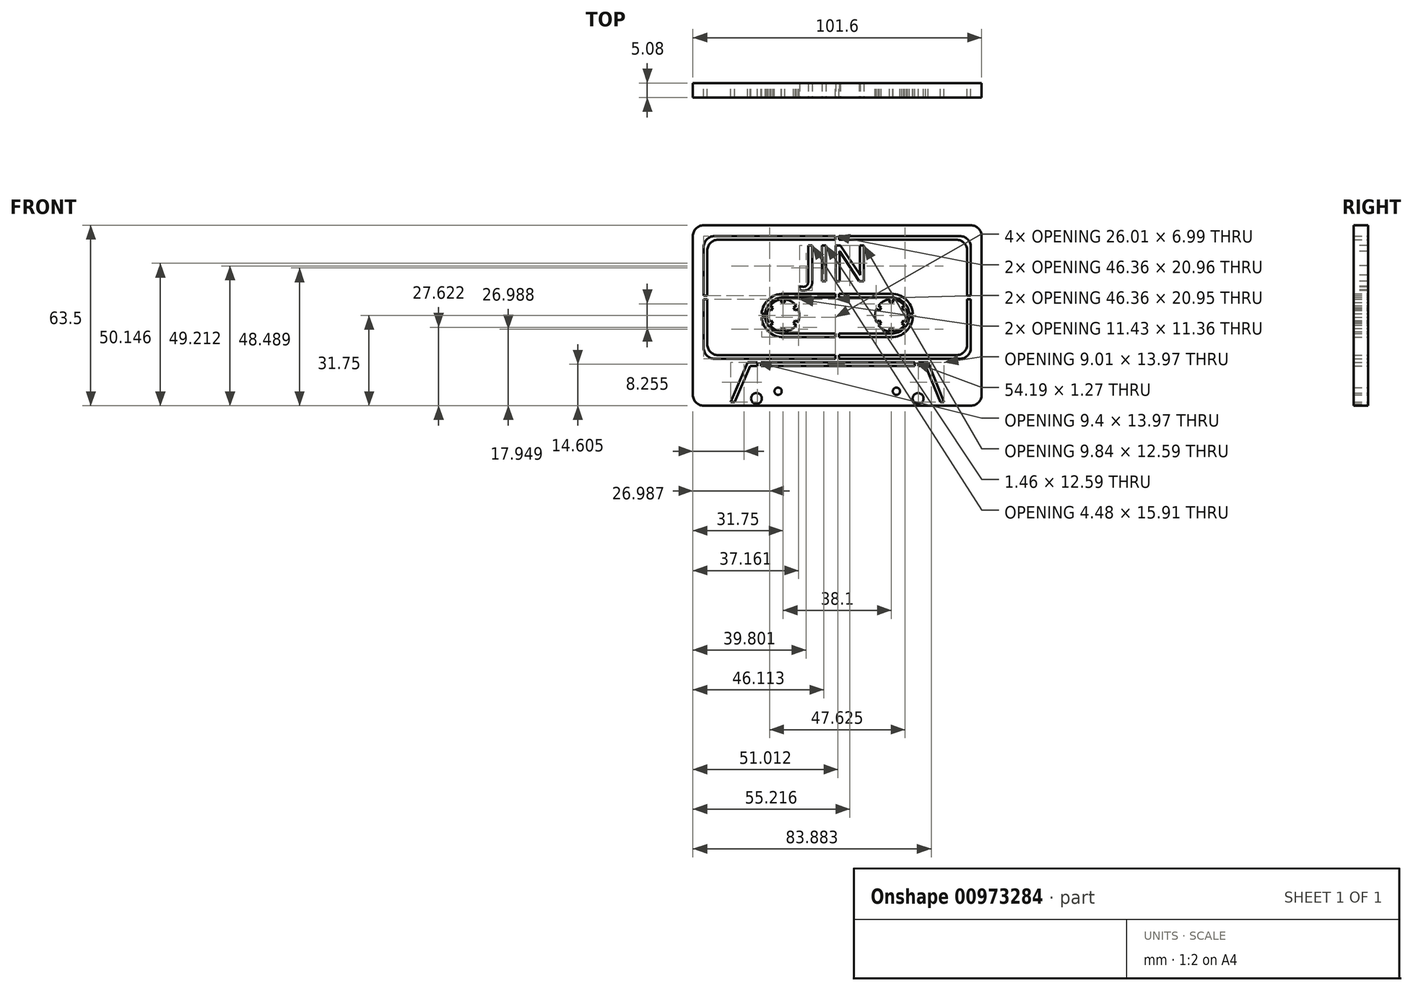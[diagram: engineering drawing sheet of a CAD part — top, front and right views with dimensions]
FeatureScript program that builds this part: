
annotation { "Feature Type Name" : "Feature", "Feature Type Description" : "" }
export const myFeature = defineFeature(function(context is Context, id is Id, definition is map)
    precondition{}
    {
        {
            var Q0;
            Q0=qCreatedBy(makeId("Front.planeOp"),FACE);
            var sketch = newSketch(context, id + "F0", { "sketchPlane" : qUnion([Q0])});
            skLineSegment(sketch, "E0.bottom", {"start": v(47, 31.75) * mm, "end": v(-47, 31.75) * mm});
            skLineSegment(sketch, "E0.top", {"start": v(47, -31.75) * mm, "end": v(-47, -31.75) * mm});
            skLineSegment(sketch, "E0.left", {"start": v(50.8, 27.94) * mm, "end": v(50.8, -27.94) * mm});
            skLineSegment(sketch, "E0.right", {"start": v(-50.8, 27.94) * mm, "end": v(-50.8, -27.94) * mm});
            skPoint(sketch, "E0.middle", {"position": v(0, 0) * mm});
            skPoint(sketch, "E1.visualSharp", {"position": v(50.8, 31.75) * mm});
            skArc(sketch, "E1.filletArc", {"start": v(50.8, 27.94) * mm, "mid": v(49.68, 30.63) * mm, "end": v(47, 31.75) * mm});
            skPoint(sketch, "E2.visualSharp", {"position": v(-50.8, 31.75) * mm});
            skArc(sketch, "E2.filletArc", {"start": v(-47, 31.75) * mm, "mid": v(-49.68, 30.63) * mm, "end": v(-50.8, 27.94) * mm});
            skPoint(sketch, "E3.visualSharp", {"position": v(-50.8, -31.75) * mm});
            skArc(sketch, "E3.filletArc", {"start": v(-50.8, -27.94) * mm, "mid": v(-49.68, -30.63) * mm, "end": v(-47, -31.75) * mm});
            skPoint(sketch, "E4.visualSharp", {"position": v(50.8, -31.75) * mm});
            skArc(sketch, "E4.filletArc", {"start": v(47, -31.75) * mm, "mid": v(49.68, -30.63) * mm, "end": v(50.8, -27.94) * mm});
            skLineSegment(sketch, "E5.bottom", {"start": v(-43.18, 27.94) * mm, "end": v(-0.64, 27.94) * mm});
            skLineSegment(sketch, "E5.top", {"start": v(-43.18, -15.24) * mm, "end": v(-0.64, -15.24) * mm});
            skLineSegment(sketch, "E5.left", {"start": v(-47, 24.13) * mm, "end": v(-47, 6.98) * mm});
            skLineSegment(sketch, "E5.right", {"start": v(47, 24.13) * mm, "end": v(47, 6.99) * mm});
            skLineSegment(sketch, "E6.bottom", {"start": v(-41.91, 26.67) * mm, "end": v(-0.63, 26.67) * mm});
            skLineSegment(sketch, "E6.top", {"start": v(-41.91, -13.97) * mm, "end": v(-0.63, -13.97) * mm});
            skLineSegment(sketch, "E6.left", {"start": v(-45.72, 22.86) * mm, "end": v(-45.72, 6.98) * mm});
            skLineSegment(sketch, "E6.right", {"start": v(45.72, 22.86) * mm, "end": v(45.72, 6.99) * mm});
            skArc(sketch, "E7.filletArc", {"start": v(47, 24.13) * mm, "mid": v(45.87, 26.82) * mm, "end": v(43.18, 27.94) * mm});
            skPoint(sketch, "E8.visualSharp", {"position": v(45.72, 26.67) * mm});
            skArc(sketch, "E8.filletArc", {"start": v(45.72, 22.86) * mm, "mid": v(44.6, 25.55) * mm, "end": v(41.91, 26.67) * mm});
            skPoint(sketch, "E9.visualSharp", {"position": v(47, -15.24) * mm});
            skArc(sketch, "E9.filletArc", {"start": v(43.18, -15.24) * mm, "mid": v(45.87, -14.12) * mm, "end": v(47, -11.43) * mm});
            skPoint(sketch, "E10.visualSharp", {"position": v(45.72, -13.97) * mm});
            skArc(sketch, "E10.filletArc", {"start": v(41.91, -13.97) * mm, "mid": v(44.6, -12.85) * mm, "end": v(45.72, -10.16) * mm});
            skPoint(sketch, "E11.visualSharp", {"position": v(-47, -15.24) * mm});
            skArc(sketch, "E11.filletArc", {"start": v(-47, -11.43) * mm, "mid": v(-45.87, -14.12) * mm, "end": v(-43.18, -15.24) * mm});
            skPoint(sketch, "E12.visualSharp", {"position": v(-45.72, -13.97) * mm});
            skArc(sketch, "E12.filletArc", {"start": v(-45.72, -10.16) * mm, "mid": v(-44.6, -12.85) * mm, "end": v(-41.91, -13.97) * mm});
            skArc(sketch, "E13.filletArc", {"start": v(-43.18, 27.94) * mm, "mid": v(-45.87, 26.82) * mm, "end": v(-47, 24.13) * mm});
            skPoint(sketch, "E14.visualSharp", {"position": v(-45.72, 26.67) * mm});
            skArc(sketch, "E14.filletArc", {"start": v(-41.91, 26.67) * mm, "mid": v(-44.6, 25.55) * mm, "end": v(-45.72, 22.86) * mm});
            skLineSegment(sketch, "E15", {"start": v(0.64, -15.24) * mm, "end": v(0.64, -13.97) * mm});
            skLineSegment(sketch, "E16", {"start": v(-0.64, -15.24) * mm, "end": v(-0.64, -13.97) * mm});
            skLineSegment(sketch, "E17.trimOffspring", {"start": v(-0.64, 26.67) * mm, "end": v(-0.64, 27.94) * mm});
            skLineSegment(sketch, "E18.trimOffspring", {"start": v(0.64, 26.67) * mm, "end": v(0.64, 27.94) * mm});
            skLineSegment(sketch, "E19.trimOffspring", {"start": v(0.63, -13.97) * mm, "end": v(41.91, -13.97) * mm});
            skLineSegment(sketch, "E20.trimOffspring", {"start": v(0.64, -15.24) * mm, "end": v(43.18, -15.24) * mm});
            skLineSegment(sketch, "E21.trimOffspring", {"start": v(0.64, 27.94) * mm, "end": v(43.18, 27.94) * mm});
            skLineSegment(sketch, "E22.trimOffspring", {"start": v(0.63, 26.67) * mm, "end": v(41.91, 26.67) * mm});
            skLineSegment(sketch, "E23", {"start": v(-47, 6.98) * mm, "end": v(-45.72, 6.99) * mm});
            skLineSegment(sketch, "E24", {"start": v(-47, 5.71) * mm, "end": v(-45.72, 5.71) * mm});
            skLineSegment(sketch, "E25.trimOffspring", {"start": v(45.72, 6.99) * mm, "end": v(47, 6.99) * mm});
            skLineSegment(sketch, "E26.trimOffspring", {"start": v(45.72, 5.72) * mm, "end": v(47, 5.72) * mm});
            skPoint(sketch, "E27.orphan", {"position": v(48.52, 5.72) * mm});
            skPoint(sketch, "E28.orphan", {"position": v(48.52, 6.99) * mm});
            skLineSegment(sketch, "E29.trimOffspring", {"start": v(47, 5.72) * mm, "end": v(47, -11.43) * mm});
            skLineSegment(sketch, "E30.trimOffspring", {"start": v(45.72, 5.72) * mm, "end": v(45.72, -10.16) * mm});
            skLineSegment(sketch, "E31.trimOffspring", {"start": v(-45.72, 5.71) * mm, "end": v(-45.72, -10.16) * mm});
            skLineSegment(sketch, "E32.trimOffspring", {"start": v(-47, 5.71) * mm, "end": v(-47, -11.43) * mm});
            skLineSegment(sketch, "E33.bottom", {"start": v(-19.05, 6.35) * mm, "end": v(-0.63, 6.35) * mm});
            skLineSegment(sketch, "E33.top", {"start": v(-19.05, -6.35) * mm, "end": v(-0.63, -6.35) * mm});
            skLineSegment(sketch, "E34.bottom", {"start": v(-19.05, 7.62) * mm, "end": v(-0.63, 7.62) * mm});
            skLineSegment(sketch, "E34.top", {"start": v(-19.05, -7.62) * mm, "end": v(-0.63, -7.62) * mm});
            skLineSegment(sketch, "E35", {"start": v(-0.63, 7.62) * mm, "end": v(-0.63, 6.35) * mm});
            skLineSegment(sketch, "E36", {"start": v(0.63, 7.62) * mm, "end": v(0.63, 6.35) * mm});
            skLineSegment(sketch, "E37.trimOffspring", {"start": v(-0.63, -6.35) * mm, "end": v(-0.63, -7.62) * mm});
            skLineSegment(sketch, "E38.trimOffspring", {"start": v(0.63, -6.35) * mm, "end": v(0.63, -7.62) * mm});
            skLineSegment(sketch, "E39.trimOffspring", {"start": v(0.64, -7.62) * mm, "end": v(19.05, -7.62) * mm});
            skLineSegment(sketch, "E40.trimOffspring", {"start": v(0.63, -6.35) * mm, "end": v(19.05, -6.35) * mm});
            skLineSegment(sketch, "E41.trimOffspring", {"start": v(0.63, 7.62) * mm, "end": v(19.05, 7.62) * mm});
            skLineSegment(sketch, "E42.trimOffspring", {"start": v(0.64, 6.35) * mm, "end": v(23.26, 6.35) * mm});
            skArc(sketch, "E43", {"start": v(-19.69, 5.68) * mm, "mid": v(-21.9, 4.95) * mm, "end": v(-23.65, 3.39) * mm});
            skArc(sketch, "E44", {"start": v(18.41, 5.68) * mm, "mid": v(16.2, 4.95) * mm, "end": v(14.45, 3.39) * mm});
            skArc(sketch, "E45", {"start": v(-19.05, 7.62) * mm, "mid": v(-24.2, 5.6) * mm, "end": v(-26.64, 0.64) * mm});
            skArc(sketch, "E46", {"start": v(-19.05, 6.35) * mm, "mid": v(-23.3, 4.7) * mm, "end": v(-25.37, 0.63) * mm});
            skArc(sketch, "E47", {"start": v(19.05, 7.62) * mm, "mid": v(24.2, 5.6) * mm, "end": v(26.64, 0.64) * mm});
            skArc(sketch, "E48", {"start": v(19.05, 6.35) * mm, "mid": v(23.3, 4.7) * mm, "end": v(25.37, 0.63) * mm});
            skLineSegment(sketch, "E49", {"start": v(-26.64, 0.64) * mm, "end": v(-25.37, 0.64) * mm});
            skLineSegment(sketch, "E50", {"start": v(-26.64, -0.64) * mm, "end": v(-25.37, -0.64) * mm});
            skArc(sketch, "E51.trimOffspring", {"start": v(-26.64, -0.64) * mm, "mid": v(-24.2, -5.6) * mm, "end": v(-19.05, -7.62) * mm});
            skArc(sketch, "E52.trimOffspring", {"start": v(-25.37, -0.64) * mm, "mid": v(-23.3, -4.7) * mm, "end": v(-19.05, -6.35) * mm});
            skLineSegment(sketch, "E53.trimOffspring", {"start": v(25.37, 0.64) * mm, "end": v(26.64, 0.64) * mm});
            skLineSegment(sketch, "E54.trimOffspring", {"start": v(25.37, -0.64) * mm, "end": v(26.64, -0.64) * mm});
            skArc(sketch, "E55.trimOffspring", {"start": v(25.37, -0.64) * mm, "mid": v(23.3, -4.7) * mm, "end": v(19.05, -6.35) * mm});
            skArc(sketch, "E56.trimOffspring", {"start": v(26.64, -0.64) * mm, "mid": v(24.2, -5.6) * mm, "end": v(19.05, -7.62) * mm});
            skLineSegment(sketch, "E57", {"start": v(-18.41, 5.68) * mm, "end": v(-18.41, 4.57) * mm});
            skLineSegment(sketch, "E58", {"start": v(-18.41, 4.57) * mm, "end": v(-19.69, 4.57) * mm});
            skLineSegment(sketch, "E59", {"start": v(-19.69, 4.57) * mm, "end": v(-19.69, 5.68) * mm});
            skLineSegment(sketch, "E60.MirrorCS", {"start": v(18.41, 5.68) * mm, "end": v(18.41, 4.57) * mm});
            skLineSegment(sketch, "E61.MirrorCS", {"start": v(18.41, 4.57) * mm, "end": v(19.69, 4.57) * mm});
            skLineSegment(sketch, "E62.MirrorCS", {"start": v(19.69, 4.57) * mm, "end": v(19.69, 5.68) * mm});
            skLineSegment(sketch, "E63.1.0", {"start": v(-23.65, 3.39) * mm, "end": v(-22.7, 2.84) * mm});
            skLineSegment(sketch, "E63.1.1", {"start": v(-22.7, 2.84) * mm, "end": v(-23.33, 1.74) * mm});
            skLineSegment(sketch, "E63.1.2", {"start": v(-23.33, 1.74) * mm, "end": v(-24.29, 2.29) * mm});
            skLineSegment(sketch, "E63.2.0", {"start": v(-24.29, -2.29) * mm, "end": v(-23.33, -1.74) * mm});
            skLineSegment(sketch, "E63.2.1", {"start": v(-23.33, -1.74) * mm, "end": v(-22.7, -2.84) * mm});
            skLineSegment(sketch, "E63.2.2", {"start": v(-22.7, -2.84) * mm, "end": v(-23.65, -3.39) * mm});
            skLineSegment(sketch, "E63.3.0", {"start": v(-19.69, -5.68) * mm, "end": v(-19.69, -4.57) * mm});
            skLineSegment(sketch, "E63.3.1", {"start": v(-19.69, -4.57) * mm, "end": v(-18.41, -4.57) * mm});
            skLineSegment(sketch, "E63.3.2", {"start": v(-18.41, -4.57) * mm, "end": v(-18.41, -5.68) * mm});
            skLineSegment(sketch, "E63.4.0", {"start": v(-14.45, -3.39) * mm, "end": v(-15.4, -2.84) * mm});
            skLineSegment(sketch, "E63.4.1", {"start": v(-15.4, -2.84) * mm, "end": v(-14.77, -1.74) * mm});
            skLineSegment(sketch, "E63.4.2", {"start": v(-14.77, -1.74) * mm, "end": v(-13.81, -2.29) * mm});
            skLineSegment(sketch, "E63.5.0", {"start": v(-13.81, 2.29) * mm, "end": v(-14.77, 1.74) * mm});
            skLineSegment(sketch, "E63.5.1", {"start": v(-14.77, 1.74) * mm, "end": v(-15.4, 2.84) * mm});
            skLineSegment(sketch, "E63.5.2", {"start": v(-15.4, 2.84) * mm, "end": v(-14.45, 3.39) * mm});
            skArc(sketch, "E64.trimOffspring", {"start": v(-14.45, 3.39) * mm, "mid": v(-16.2, 4.95) * mm, "end": v(-18.41, 5.68) * mm});
            skArc(sketch, "E65.trimOffspring", {"start": v(-13.81, -2.29) * mm, "mid": v(-13.33, 0) * mm, "end": v(-13.81, 2.29) * mm});
            skArc(sketch, "E66.trimOffspring", {"start": v(-18.41, -5.68) * mm, "mid": v(-16.2, -4.95) * mm, "end": v(-14.45, -3.39) * mm});
            skArc(sketch, "E67.trimOffspring", {"start": v(-23.65, -3.39) * mm, "mid": v(-21.9, -4.95) * mm, "end": v(-19.69, -5.68) * mm});
            skArc(sketch, "E68.trimOffspring", {"start": v(-24.29, 2.29) * mm, "mid": v(-24.77, 0) * mm, "end": v(-24.29, -2.29) * mm});
            skLineSegment(sketch, "E69.1.0", {"start": v(15.4, 2.84) * mm, "end": v(14.45, 3.39) * mm});
            skLineSegment(sketch, "E69.1.1", {"start": v(14.77, 1.74) * mm, "end": v(15.4, 2.84) * mm});
            skLineSegment(sketch, "E69.1.2", {"start": v(13.81, 2.29) * mm, "end": v(14.77, 1.74) * mm});
            skLineSegment(sketch, "E69.2.0", {"start": v(14.77, -1.74) * mm, "end": v(13.81, -2.29) * mm});
            skLineSegment(sketch, "E69.2.1", {"start": v(15.4, -2.84) * mm, "end": v(14.77, -1.74) * mm});
            skLineSegment(sketch, "E69.2.2", {"start": v(14.45, -3.39) * mm, "end": v(15.4, -2.84) * mm});
            skLineSegment(sketch, "E69.3.0", {"start": v(18.41, -4.57) * mm, "end": v(18.41, -5.68) * mm});
            skLineSegment(sketch, "E69.3.1", {"start": v(19.69, -4.57) * mm, "end": v(18.41, -4.57) * mm});
            skLineSegment(sketch, "E69.3.2", {"start": v(19.69, -5.68) * mm, "end": v(19.69, -4.57) * mm});
            skLineSegment(sketch, "E69.4.0", {"start": v(22.7, -2.84) * mm, "end": v(23.65, -3.39) * mm});
            skLineSegment(sketch, "E69.4.1", {"start": v(23.33, -1.74) * mm, "end": v(22.7, -2.84) * mm});
            skLineSegment(sketch, "E69.4.2", {"start": v(24.29, -2.29) * mm, "end": v(23.33, -1.74) * mm});
            skLineSegment(sketch, "E69.5.0", {"start": v(23.33, 1.74) * mm, "end": v(24.29, 2.29) * mm});
            skLineSegment(sketch, "E69.5.1", {"start": v(22.7, 2.84) * mm, "end": v(23.33, 1.74) * mm});
            skLineSegment(sketch, "E69.5.2", {"start": v(23.65, 3.39) * mm, "end": v(22.7, 2.84) * mm});
            skArc(sketch, "E70.trimOffspring", {"start": v(23.65, 3.39) * mm, "mid": v(21.9, 4.95) * mm, "end": v(19.69, 5.68) * mm});
            skArc(sketch, "E71.trimOffspring", {"start": v(24.29, -2.29) * mm, "mid": v(24.77, 0) * mm, "end": v(24.29, 2.29) * mm});
            skArc(sketch, "E72.trimOffspring", {"start": v(19.69, -5.68) * mm, "mid": v(21.9, -4.95) * mm, "end": v(23.65, -3.39) * mm});
            skArc(sketch, "E73.trimOffspring", {"start": v(14.45, -3.39) * mm, "mid": v(16.2, -4.95) * mm, "end": v(18.41, -5.68) * mm});
            skArc(sketch, "E74.trimOffspring", {"start": v(13.81, 2.29) * mm, "mid": v(13.33, 0) * mm, "end": v(13.81, -2.29) * mm});
            skLineSegment(sketch, "E75", {"start": v(-37.55, -30.48) * mm, "end": v(-31.53, -16.51) * mm});
            skLineSegment(sketch, "E76", {"start": v(-31.53, -16.51) * mm, "end": v(-28.15, -16.51) * mm});
            skLineSegment(sketch, "E77", {"start": v(31.97, -16.5) * mm, "end": v(37.59, -30.48) * mm});
            skLineSegment(sketch, "E78", {"start": v(-36.17, -30.48) * mm, "end": v(-30.7, -17.78) * mm});
            skLineSegment(sketch, "E79", {"start": v(-30.7, -17.78) * mm, "end": v(-28.15, -17.78) * mm});
            skLineSegment(sketch, "E80", {"start": v(31.12, -17.78) * mm, "end": v(36.22, -30.48) * mm});
            skLineSegment(sketch, "E81", {"start": v(-37.55, -30.48) * mm, "end": v(-36.17, -30.48) * mm});
            skLineSegment(sketch, "E82.trimOffspring", {"start": v(36.22, -30.48) * mm, "end": v(37.59, -30.48) * mm});
            skPoint(sketch, "E83.orphan", {"position": v(-38.1, -31.75) * mm});
            skPoint(sketch, "E84.orphan", {"position": v(38.1, -31.75) * mm});
            skLineSegment(sketch, "E85", {"start": v(-28.15, -17.78) * mm, "end": v(-28.15, -16.51) * mm});
            skLineSegment(sketch, "E86", {"start": v(-26.88, -16.51) * mm, "end": v(-26.88, -17.78) * mm});
            skLineSegment(sketch, "E87.trimOffspring", {"start": v(-26.88, -16.51) * mm, "end": v(27.3, -16.5) * mm});
            skLineSegment(sketch, "E88.trimOffspring", {"start": v(-26.88, -17.78) * mm, "end": v(27.3, -17.78) * mm});
            skLineSegment(sketch, "E89.MirrorCS", {"start": v(27.3, -16.5) * mm, "end": v(27.3, -17.78) * mm});
            skLineSegment(sketch, "E90.MirrorCS", {"start": v(28.58, -17.78) * mm, "end": v(28.58, -16.5) * mm});
            skLineSegment(sketch, "E91.trimOffspring", {"start": v(28.58, -16.5) * mm, "end": v(31.97, -16.5) * mm});
            skLineSegment(sketch, "E92.trimOffspring", {"start": v(28.58, -17.78) * mm, "end": v(31.12, -17.78) * mm});
            skCircle(sketch, "E93", {"center": v(-28.44, -29.21) * mm, "radius": 1.9 * mm});
            skCircle(sketch, "E94", {"center": v(-20.82, -26.67) * mm, "radius": 1.27 * mm});
            skCircle(sketch, "E95.MirrorC", {"center": v(20.82, -26.67) * mm, "radius": 1.27 * mm});
            skCircle(sketch, "E96.MirrorC", {"center": v(28.44, -29.21) * mm, "radius": 1.9 * mm});
            skSolve(sketch);
        }
        {
            var Q0;
            Q0 = qSketchRegion(id + "F0", true);
            extrude(context, id + "F1", {"entities" : qUnion([Q0]), "depth" : 5.08 * mm, "offsetDistance" : 25.4 * mm});
        }
        {
            var Q0;
            Q0=makeQuery(id+"F1.opExtrude","CAP_FACE",FACE,{"disambiguationData":[OSD([sQuery(id+"F0.wireOp",EDGE,"E0.bottom"),sQuery(id+"F0.wireOp",EDGE,"E0.top"),sQuery(id+"F0.wireOp",EDGE,"E0.left"),sQuery(id+"F0.wireOp",EDGE,"E0.right"),sQuery(id+"F0.wireOp",EDGE,"E1.filletArc"),sQuery(id+"F0.wireOp",EDGE,"E2.filletArc"),sQuery(id+"F0.wireOp",EDGE,"E3.filletArc"),sQuery(id+"F0.wireOp",EDGE,"E4.filletArc"),sQuery(id+"F0.wireOp",EDGE,"E5.bottom"),sQuery(id+"F0.wireOp",EDGE,"E5.top"),sQuery(id+"F0.wireOp",EDGE,"E5.left"),sQuery(id+"F0.wireOp",EDGE,"E5.right"),sQuery(id+"F0.wireOp",EDGE,"E6.bottom"),sQuery(id+"F0.wireOp",EDGE,"E6.top"),sQuery(id+"F0.wireOp",EDGE,"E6.left"),sQuery(id+"F0.wireOp",EDGE,"E6.right"),sQuery(id+"F0.wireOp",EDGE,"E7.filletArc"),sQuery(id+"F0.wireOp",EDGE,"E8.filletArc"),sQuery(id+"F0.wireOp",EDGE,"E9.filletArc"),sQuery(id+"F0.wireOp",EDGE,"E10.filletArc"),sQuery(id+"F0.wireOp",EDGE,"E11.filletArc"),sQuery(id+"F0.wireOp",EDGE,"E12.filletArc"),sQuery(id+"F0.wireOp",EDGE,"E13.filletArc"),sQuery(id+"F0.wireOp",EDGE,"E14.filletArc"),sQuery(id+"F0.wireOp",EDGE,"E15"),sQuery(id+"F0.wireOp",EDGE,"E16"),sQuery(id+"F0.wireOp",EDGE,"E17.trimOffspring"),sQuery(id+"F0.wireOp",EDGE,"E18.trimOffspring"),sQuery(id+"F0.wireOp",EDGE,"E19.trimOffspring"),sQuery(id+"F0.wireOp",EDGE,"E20.trimOffspring"),sQuery(id+"F0.wireOp",EDGE,"E21.trimOffspring"),sQuery(id+"F0.wireOp",EDGE,"E22.trimOffspring"),sQuery(id+"F0.wireOp",EDGE,"E23"),sQuery(id+"F0.wireOp",EDGE,"E24"),sQuery(id+"F0.wireOp",EDGE,"E25.trimOffspring"),sQuery(id+"F0.wireOp",EDGE,"E26.trimOffspring"),sQuery(id+"F0.wireOp",EDGE,"E29.trimOffspring"),sQuery(id+"F0.wireOp",EDGE,"E30.trimOffspring"),sQuery(id+"F0.wireOp",EDGE,"E31.trimOffspring"),sQuery(id+"F0.wireOp",EDGE,"E32.trimOffspring"),sQuery(id+"F0.wireOp",EDGE,"E33.bottom"),sQuery(id+"F0.wireOp",EDGE,"E33.top"),sQuery(id+"F0.wireOp",EDGE,"E34.bottom"),sQuery(id+"F0.wireOp",EDGE,"E34.top"),sQuery(id+"F0.wireOp",EDGE,"E35"),sQuery(id+"F0.wireOp",EDGE,"E36"),sQuery(id+"F0.wireOp",EDGE,"E37.trimOffspring"),sQuery(id+"F0.wireOp",EDGE,"E38.trimOffspring"),sQuery(id+"F0.wireOp",EDGE,"E39.trimOffspring"),sQuery(id+"F0.wireOp",EDGE,"E40.trimOffspring"),sQuery(id+"F0.wireOp",EDGE,"E41.trimOffspring"),sQuery(id+"F0.wireOp",EDGE,"E42.trimOffspring"),sQuery(id+"F0.wireOp",EDGE,"E43"),sQuery(id+"F0.wireOp",EDGE,"E44"),sQuery(id+"F0.wireOp",EDGE,"E45"),sQuery(id+"F0.wireOp",EDGE,"E46"),sQuery(id+"F0.wireOp",EDGE,"E47"),sQuery(id+"F0.wireOp",EDGE,"E48"),sQuery(id+"F0.wireOp",EDGE,"E49"),sQuery(id+"F0.wireOp",EDGE,"E50"),sQuery(id+"F0.wireOp",EDGE,"E51.trimOffspring"),sQuery(id+"F0.wireOp",EDGE,"E52.trimOffspring"),sQuery(id+"F0.wireOp",EDGE,"E53.trimOffspring"),sQuery(id+"F0.wireOp",EDGE,"E54.trimOffspring"),sQuery(id+"F0.wireOp",EDGE,"E55.trimOffspring"),sQuery(id+"F0.wireOp",EDGE,"E56.trimOffspring"),sQuery(id+"F0.wireOp",EDGE,"E57"),sQuery(id+"F0.wireOp",EDGE,"E58"),sQuery(id+"F0.wireOp",EDGE,"E59"),sQuery(id+"F0.wireOp",EDGE,"E60.MirrorCS"),sQuery(id+"F0.wireOp",EDGE,"E61.MirrorCS"),sQuery(id+"F0.wireOp",EDGE,"E62.MirrorCS"),sQuery(id+"F0.wireOp",EDGE,"E63.1.0"),sQuery(id+"F0.wireOp",EDGE,"E63.1.1"),sQuery(id+"F0.wireOp",EDGE,"E63.1.2"),sQuery(id+"F0.wireOp",EDGE,"E63.2.0"),sQuery(id+"F0.wireOp",EDGE,"E63.2.1"),sQuery(id+"F0.wireOp",EDGE,"E63.2.2"),sQuery(id+"F0.wireOp",EDGE,"E63.3.0"),sQuery(id+"F0.wireOp",EDGE,"E63.3.1"),sQuery(id+"F0.wireOp",EDGE,"E63.3.2"),sQuery(id+"F0.wireOp",EDGE,"E63.4.0"),sQuery(id+"F0.wireOp",EDGE,"E63.4.1"),sQuery(id+"F0.wireOp",EDGE,"E63.4.2"),sQuery(id+"F0.wireOp",EDGE,"E63.5.0"),sQuery(id+"F0.wireOp",EDGE,"E63.5.1"),sQuery(id+"F0.wireOp",EDGE,"E63.5.2"),sQuery(id+"F0.wireOp",EDGE,"E64.trimOffspring"),sQuery(id+"F0.wireOp",EDGE,"E65.trimOffspring"),sQuery(id+"F0.wireOp",EDGE,"E66.trimOffspring"),sQuery(id+"F0.wireOp",EDGE,"E67.trimOffspring"),sQuery(id+"F0.wireOp",EDGE,"E68.trimOffspring"),sQuery(id+"F0.wireOp",EDGE,"E69.1.0"),sQuery(id+"F0.wireOp",EDGE,"E69.1.1"),sQuery(id+"F0.wireOp",EDGE,"E69.1.2"),sQuery(id+"F0.wireOp",EDGE,"E69.2.0"),sQuery(id+"F0.wireOp",EDGE,"E69.2.1"),sQuery(id+"F0.wireOp",EDGE,"E69.2.2"),sQuery(id+"F0.wireOp",EDGE,"E69.3.0"),sQuery(id+"F0.wireOp",EDGE,"E69.3.1"),sQuery(id+"F0.wireOp",EDGE,"E69.3.2"),sQuery(id+"F0.wireOp",EDGE,"E69.4.0"),sQuery(id+"F0.wireOp",EDGE,"E69.4.1"),sQuery(id+"F0.wireOp",EDGE,"E69.4.2"),sQuery(id+"F0.wireOp",EDGE,"E69.5.0"),sQuery(id+"F0.wireOp",EDGE,"E69.5.1"),sQuery(id+"F0.wireOp",EDGE,"E69.5.2"),sQuery(id+"F0.wireOp",EDGE,"E70.trimOffspring"),sQuery(id+"F0.wireOp",EDGE,"E71.trimOffspring"),sQuery(id+"F0.wireOp",EDGE,"E72.trimOffspring"),sQuery(id+"F0.wireOp",EDGE,"E73.trimOffspring"),sQuery(id+"F0.wireOp",EDGE,"E74.trimOffspring"),sQuery(id+"F0.wireOp",EDGE,"E75"),sQuery(id+"F0.wireOp",EDGE,"E76"),sQuery(id+"F0.wireOp",EDGE,"E77"),sQuery(id+"F0.wireOp",EDGE,"E78"),sQuery(id+"F0.wireOp",EDGE,"E79"),sQuery(id+"F0.wireOp",EDGE,"E80"),sQuery(id+"F0.wireOp",EDGE,"E81"),sQuery(id+"F0.wireOp",EDGE,"E82.trimOffspring"),sQuery(id+"F0.wireOp",EDGE,"E85"),sQuery(id+"F0.wireOp",EDGE,"E86"),sQuery(id+"F0.wireOp",EDGE,"E87.trimOffspring"),sQuery(id+"F0.wireOp",EDGE,"E88.trimOffspring"),sQuery(id+"F0.wireOp",EDGE,"E89.MirrorCS"),sQuery(id+"F0.wireOp",EDGE,"E90.MirrorCS"),sQuery(id+"F0.wireOp",EDGE,"E91.trimOffspring"),sQuery(id+"F0.wireOp",EDGE,"E92.trimOffspring"),sQuery(id+"F0.wireOp",EDGE,"E93"),sQuery(id+"F0.wireOp",EDGE,"E94"),sQuery(id+"F0.wireOp",EDGE,"E95.MirrorC"),sQuery(id+"F0.wireOp",EDGE,"E96.MirrorC")])],"isStart":false});
            var sketch = newSketch(context, id + "F2", { "sketchPlane" : qUnion([Q0])});
            skText(sketch, "E97", { "text": "JIN", "fontName": "OpenSans-Regular.ttf"});
            const initialGuessF2  = {"E97": [-0.01186, 0.0121, 1, 0, 0.0127]};
            skSetInitialGuess(sketch, initialGuessF2);
            skSolve(sketch);
        }
        {
            var Q0;
            Q0 = qSketchRegion(id + "F2", true);
            extrude(context, id + "F3", {"entities" : qUnion([Q0]), "operationType" : NewBodyOperationType.REMOVE, "oppositeDirection" : true, "depth" : 25.4 * mm, "offsetDistance" : 25.4 * mm});
        }
    });
